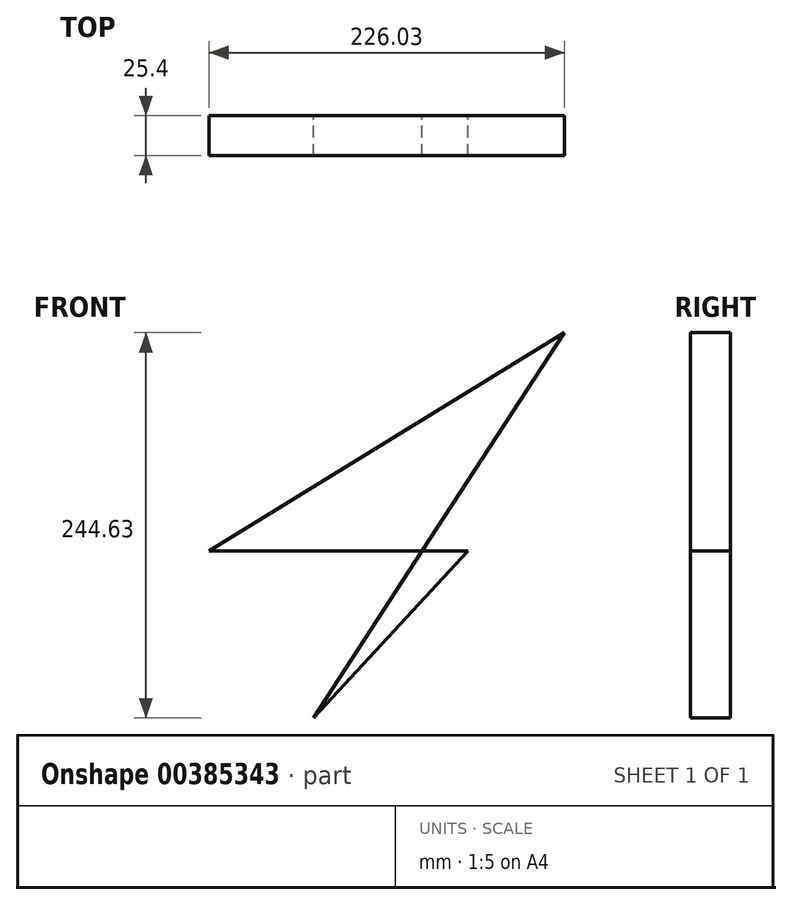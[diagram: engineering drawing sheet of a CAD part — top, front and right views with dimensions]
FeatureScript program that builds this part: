
annotation { "Feature Type Name" : "Feature", "Feature Type Description" : "" }
export const myFeature = defineFeature(function(context is Context, id is Id, definition is map)
    precondition{}
    {
        {
            var Q0;
            Q0=qCreatedBy(makeId("Front.planeOp"),FACE);
            var sketch = newSketch(context, id + "F0", { "sketchPlane" : qUnion([Q0])});
            skLineSegment(sketch, "E0", {"start": v(-66.5, 64.31) * mm, "end": v(98.01, 64.31) * mm});
            skLineSegment(sketch, "E1", {"start": v(98.01, 64.31) * mm, "end": v(0, -41.56) * mm});
            skLineSegment(sketch, "E2", {"start": v(0, -41.56) * mm, "end": v(159.52, 203.07) * mm});
            skLineSegment(sketch, "E3", {"start": v(159.52, 203.07) * mm, "end": v(-66.5, 64.31) * mm});
            skSolve(sketch);
        }
        {
            var Q0;
            Q0 = qSketchRegion(id + "F0", true);
            extrude(context, id + "F1", {"entities" : qUnion([Q0]), "depth" : 25.4 * mm});
        }
    });
